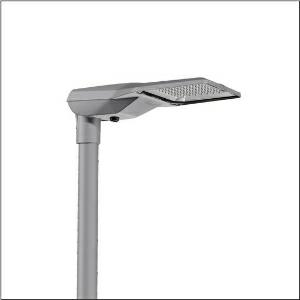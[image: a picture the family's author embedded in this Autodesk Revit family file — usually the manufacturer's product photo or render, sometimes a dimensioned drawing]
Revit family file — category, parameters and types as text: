
# Revit family: streetlight_sl_21_iq_midi___p0_5a_5xe3v31u08mb_699d
name_source: partatom
category: Lighting Fixtures
units: mm (PartAtom-declared; Revit-internal decimal feet)

## family parameters
Cut with Voids When Loaded = No
Host = Face
Light Source = No
Part Type = Normal
Room Calculation Point = No
Round Connector Dimension = Use Diameter
Shared = No

## types (1)
- --- (1 x LED, 18020 lm, 129.3 W, 3000K)
    Apparent Load = 129 VA
    CIE Flux Codes = 37 73 96 100 100
    Color Rendering = 70
    Color Temperature = 3000K
    Default Elevation = 1800 mm
    Description = Streetlight SL 21 iQ midi, mast luminaire, primary light control with lens, of PMMA, primary optical cover: cover, of toughened safety glass, transparent, light distribution: P0.5a, light emission: direct distribution, primary light characteristic: asymmetric, installation type: post-top, side-entry, LED, High Power LED, rated luminous flux: 18.020lm, luminous efficacy: 139lm/W, light colour: 730, colour temperature: 3000K, control gear: iQ-Street Remote, D4i with power reduction, control: pre-setting: logarithmic dimming characteristic, Street-Remote, Auto-Match, Temp-Guard, Lumen-Switch, Night-Set, Smart-Wire, Light-Fading, Desk-Remote (wireless, voltage-free reading and setting of iQ features in the workshop via application-optimized NFC function/RFID function), optimised constant luminous flux control (CLO 2.0), mains connection: 230..240V, AC, 50/60Hz, start of lifetime: 129W, end of service life: 142W, reduction: 56W, luminaire housing, of diecast aluminium, powder-coated, Siteco® metallic grey (DB 702S), corrosivity category C5 mid according to DIN EN ISO 12944, please order mast flange separately, inclination adjustable: 0°, 5°, 10°, 15°, sealing non-destructively replaceable, multi-level sealing system, length: 644mm, width: 335mm, height: 110mm, mast flange for spigot size: 42mm (side-entry): 5XC10008XM4, 60/48mm (side-entry/post-top): 5XC10108XM2, 76/60mm (side-entry/post-top): 5XC10108XM1, mounting height: 4..8m, Smart Interface below, protection rating (complete): IP66, insulation class (complete): insulation class II (safety insulation), certification: CE, ENEC, ENEC+, VDE, impact resistance: IK10, permissible operating ambient temperature for outdoor applications: -40..+50°C, standard-compliant lighting for roads and squares, packaging unit: 1 piece

Light Distribution: P0.5a
    Height = 111 mm
    Lamp = 1 x LED
    Lamp Light Flux = 18020 lm
    Lamp Power = 129.3 W
    Lamp count = 1
    Length = 644 mm
    Luminous efficacy = 139 lm/W
    Manufacturer = Siteco
    ModVariant = No
    Model = 5XE3V31U08MB
    Number of Poles = 1
    OnlyDefault = Yes
    Power Factor = 1
    Product Name = Streetlight SL 21 iQ midi | P0.5a
    Product group = mast luminaire | pylon top
    ProductGroupID = 6100
    Protection Class = Protection class II
    Protection Degree = IP 66
    RLX_Detail_Level = 1
    RLX_Emergency_Light_Flux = 0 lm
    RLX_Emergency_Type = 0
    RLX_Emergency_Type_DB = No
    RlxData = <blob elided: 26749 chars, md5=7f4e265e>
    Socket = socket
    Standby Power = 0 W
    System Light Flux = 18021 lm
    System Power = 129 W
    Type Comments = factory setting: luminous flux: 100 % | dim-lin: 254 | 672 mA
    Type Image = l_1004300.jpg
    URL = http://relux.com
    VarID = @adj_070518
    Voltage = 0 V
    Weight = 0.00 kg
    Width = 336 mm

## geometry (parser evidence)
native form markers: Blend x4, Sweep x12
no freeform markers — native parametric forms only
